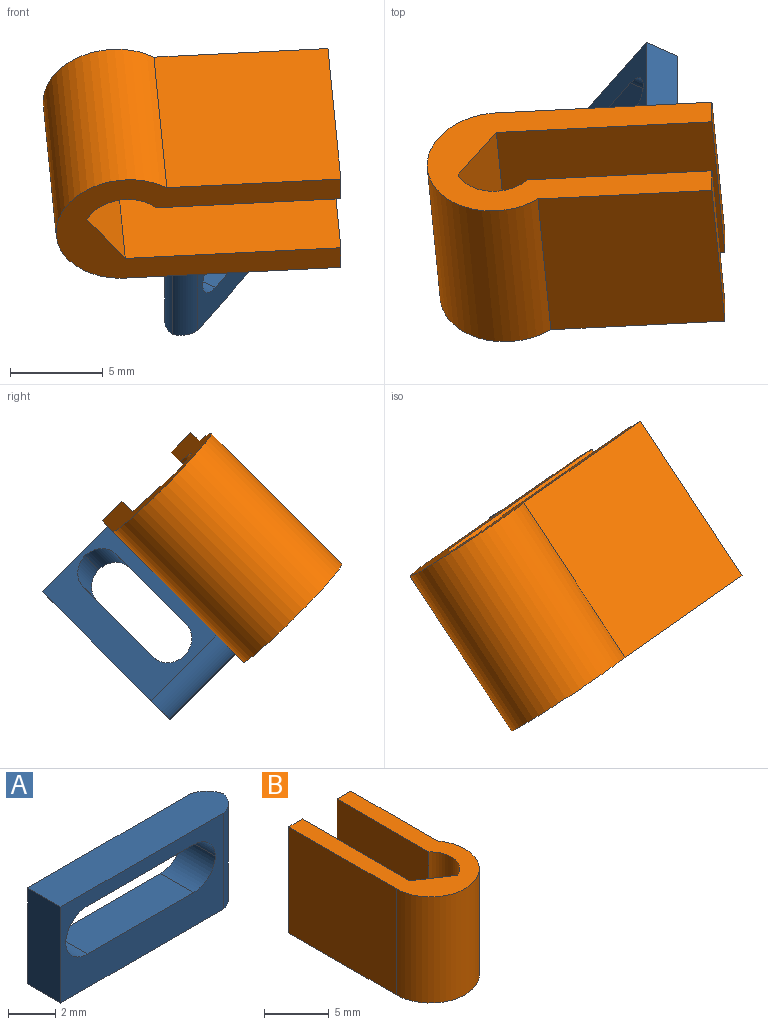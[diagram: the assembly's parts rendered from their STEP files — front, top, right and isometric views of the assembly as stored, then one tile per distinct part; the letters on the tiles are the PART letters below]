
ASSEMBLY  parts=2 mates=1
PART A: 13 faces, bbox 10.8x2x5 mm
  f0: plane 9.8x5mm, normal (0,-1,0), area 28mm2, adj f2,f3,f4,f6,f7,f8,f9,f10
  f1: plane 9.8x5mm, normal (0,1,0), area 28mm2, adj f2,f3,f5,f6,f7,f8,f9,f10
  f2: plane 10.8x2mm, normal (0,0,1), area 21mm2, adj f0,f1,f4,f5,f12
  f3: plane 10.8x2mm, normal (0,0,-1), area 21mm2, adj f0,f1,f4,f5,f12
  f4: cylinder r=1.31mm len=5mm, axis (0,0,-1), area 7.5mm2, adj f0,f2,f3,f5
  f5: cylinder r=1.31mm len=5mm, axis (0,0,-1), area 7.5mm2, adj f1,f2,f3,f4
  f6: plane 6.4x2mm, normal (0,0,1), area 12.8mm2, adj f0,f1,f9,f11
  f7: plane 6.4x2mm, normal (0,0,-1), area 12.8mm2, adj f0,f1,f8,f10
  f8: cylinder r=1.3mm len=2mm, axis (0,-1,0), area 4mm2, adj f0,f1,f7,f9
  f9: cylinder r=1.3mm len=2mm, axis (0,1,0), area 4mm2, adj f0,f1,f6,f8
  f10: cylinder r=1.3mm len=2mm, axis (0,1,0), area 4mm2, adj f0,f1,f7,f11
  f11: cylinder r=1.3mm len=2mm, axis (0,-1,0), area 4mm2, adj f0,f1,f6,f10
  f12: plane 5x2mm, normal (-1,0,0), area 10mm2, adj f0,f1,f2,f3
PART B: 11 faces, bbox 7.5x15.4x10 mm
  f0: plane 11.68x10mm, normal (-1,0,0), area 116.8mm2, adj f1,f8,f9,f10
  f1: cylinder r=3.75mm len=10mm, axis (0,0,-1), area 141.9mm2, adj f0,f2,f9,f10
  f2: plane 10x9.43mm, normal (1,0,0), area 94.3mm2, adj f1,f3,f9,f10
  f3: plane 10x1.5mm, normal (0,1,0), area 15mm2, adj f2,f4,f9,f10
  f4: plane 10x10mm, normal (-1,0,0), area 100mm2, adj f3,f5,f9,f10
  f5: cylinder r=2.25mm len=10mm, axis (0,0,-1), area 45.4mm2, adj f4,f6,f9,f10
  f6: plane 10x3.11mm, normal (0.56,0.83,0), area 37.4mm2, adj f5,f7,f9,f10
  f7: plane 11.68x10mm, normal (1,0,0), area 116.8mm2, adj f6,f8,f9,f10
  f8: plane 10x1.5mm, normal (0,1,0), area 15mm2, adj f0,f7,f9,f10
  f9: plane 15.43x7.5mm, normal (0,0,1), area 52.1mm2, adj f0,f1,f2,f3,f4,f5,f6,f7
  f10: plane 15.43x7.5mm, normal (0,0,-1), area 52.1mm2, adj f0,f1,f2,f3,f4,f5,f6,f7
PLACE A rot(axis=(0.21,0.37,-0.9),126.8deg) t=(-16.18,-5.08,0.75)mm
PLACE B rot(axis=(-0.33,-0.39,-0.86),97deg) t=(-21.9,-15.36,2.85)mm
MATE revolute B.f0 <-> A.f2  axis (0,0.71,-0.71) through (-16.42,-8.89,4.01)mm
